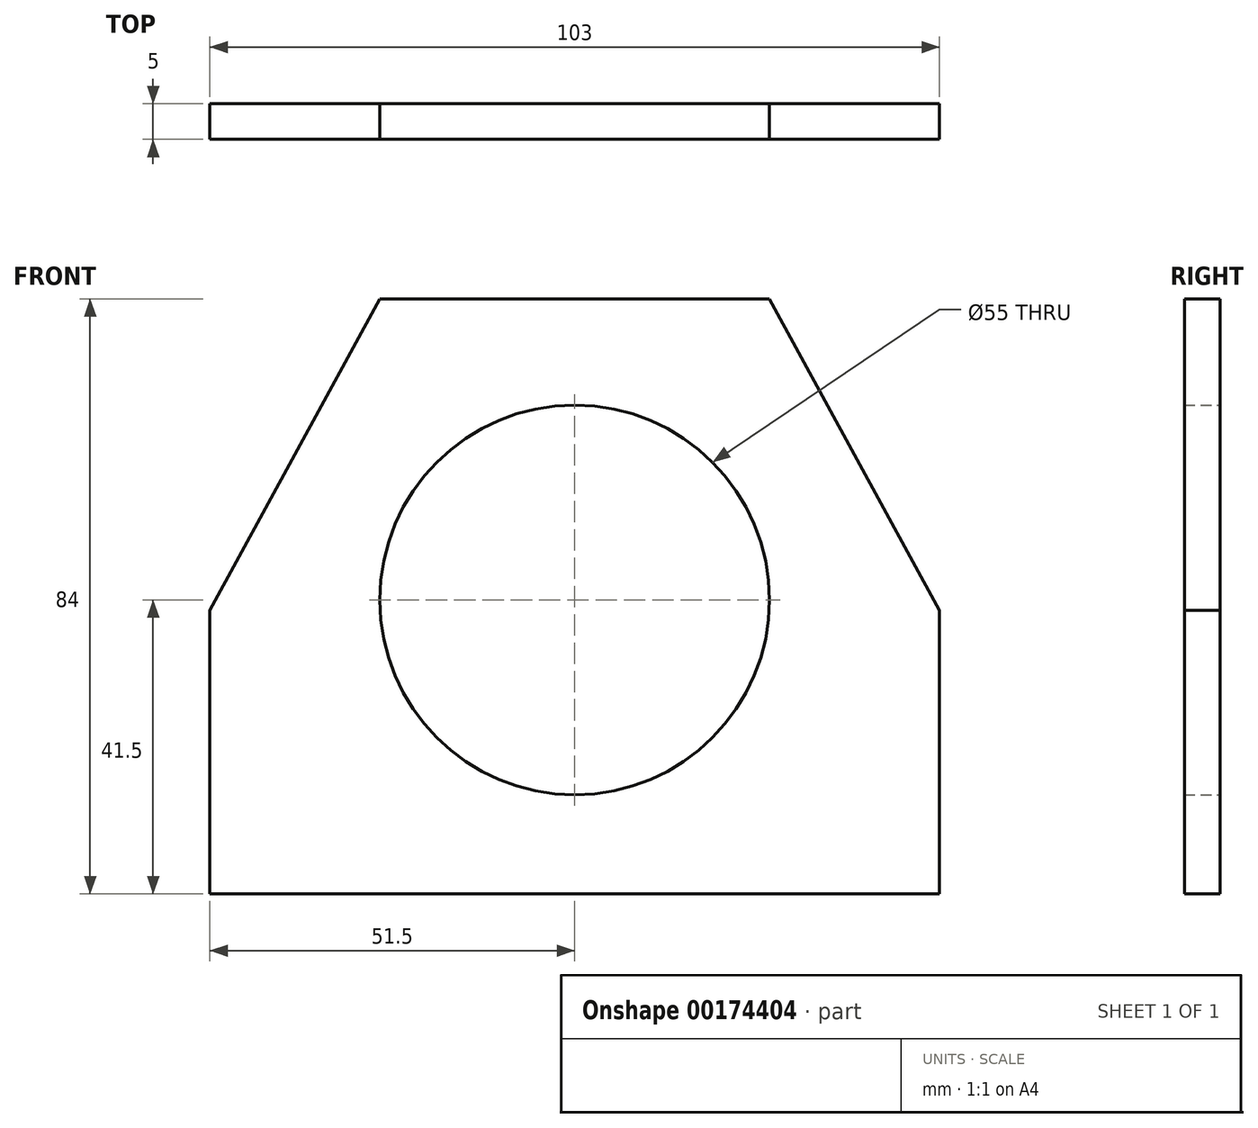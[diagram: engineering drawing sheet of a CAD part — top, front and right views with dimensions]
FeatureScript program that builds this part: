
annotation { "Feature Type Name" : "Feature", "Feature Type Description" : "" }
export const myFeature = defineFeature(function(context is Context, id is Id, definition is map)
    precondition{}
    {
        {
            var Q0;
            Q0=qCreatedBy(makeId("Front.planeOp"),FACE);
            var sketch = newSketch(context, id + "F0", { "sketchPlane" : qUnion([Q0])});
            skCircle(sketch, "E0", {"center": v(0, 0) * mm, "radius": 27.5 * mm});
            skLineSegment(sketch, "E1", {"start": v(51.5, -41.5) * mm, "end": v(-51.5, -41.5) * mm});
            skLineSegment(sketch, "E2", {"start": v(-51.5, -41.5) * mm, "end": v(-51.5, -1.5) * mm});
            skLineSegment(sketch, "E3", {"start": v(-51.5, -1.5) * mm, "end": v(-27.5, 42.5) * mm});
            skLineSegment(sketch, "E4", {"start": v(-27.5, 42.5) * mm, "end": v(27.5, 42.5) * mm});
            skLineSegment(sketch, "E5.MirrorCS", {"start": v(51.5, -41.5) * mm, "end": v(51.5, -1.5) * mm});
            skLineSegment(sketch, "E6.MirrorCS", {"start": v(51.5, -1.5) * mm, "end": v(27.5, 42.5) * mm});
            skLineSegment(sketch, "E7", {"start": v(0, -27.5) * mm, "end": v(0, -41.5) * mm, "construction": true});
            skPoint(sketch, "E7.startSnap0", {"position": v(0, -41.5) * mm});
            skLineSegment(sketch, "E8", {"start": v(0, 27.5) * mm, "end": v(0, 42.5) * mm, "construction": true});
            skSolve(sketch);
        }
        {
            var Q0;
            Q0 = qSketchRegion(id + "F0", true);
            extrude(context, id + "F1", {"entities" : qUnion([Q0]), "depth" : 5 * mm});
        }
    });
